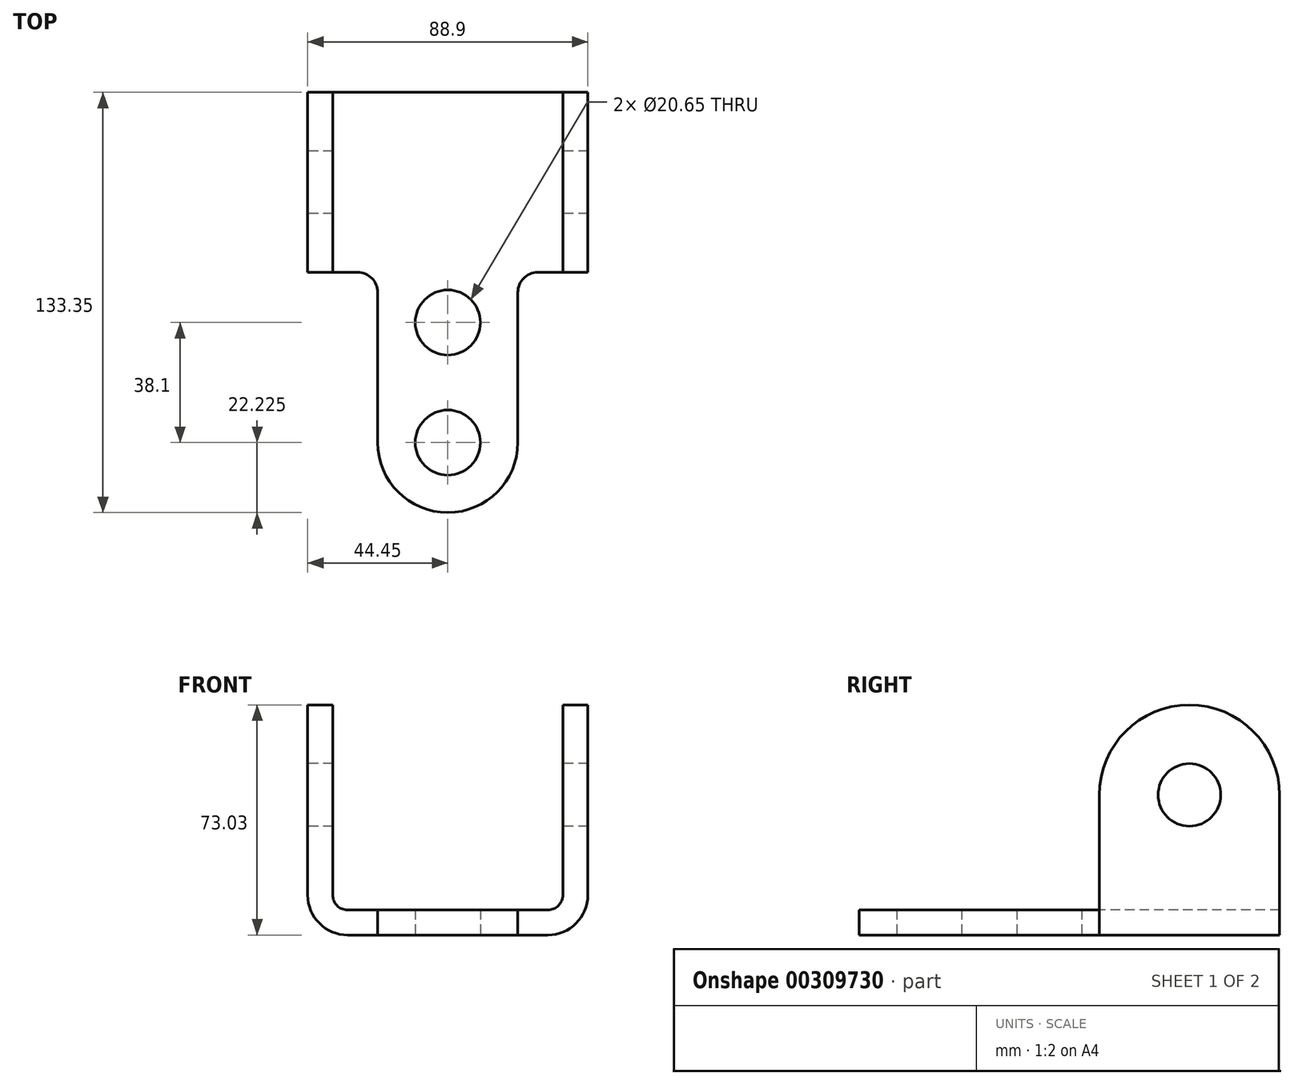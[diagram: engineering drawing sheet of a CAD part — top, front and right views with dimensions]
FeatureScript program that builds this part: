
annotation { "Feature Type Name" : "Feature", "Feature Type Description" : "" }
export const myFeature = defineFeature(function(context is Context, id is Id, definition is map)
    precondition{}
    {
        {
            var Q0;
            Q0=qCreatedBy(makeId("Right.planeOp"),FACE);
            var sketch = newSketch(context, id + "F0", { "sketchPlane" : qUnion([Q0])});
            skLineSegment(sketch, "E0", {"start": v(0, 0) * mm, "end": v(0, 44.45) * mm});
            skLineSegment(sketch, "E1", {"start": v(28.58, 73.03) * mm, "end": v(28.58, 73.03) * mm});
            skLineSegment(sketch, "E2", {"start": v(57.15, 44.45) * mm, "end": v(57.15, 0) * mm});
            skPoint(sketch, "E3.orphan", {"position": v(57.15, 0) * mm});
            skPoint(sketch, "E4.visualSharp", {"position": v(0, 73.03) * mm});
            skArc(sketch, "E4.filletArc", {"start": v(28.58, 73.03) * mm, "mid": v(8.37, 64.66) * mm, "end": v(0, 44.45) * mm});
            skPoint(sketch, "E5.visualSharp", {"position": v(57.15, 73.03) * mm});
            skArc(sketch, "E5.filletArc", {"start": v(57.15, 44.45) * mm, "mid": v(48.78, 64.66) * mm, "end": v(28.58, 73.03) * mm});
            skCircle(sketch, "E6", {"center": v(28.58, 44.45) * mm, "radius": 9.92 * mm});
            skLineSegment(sketch, "E7", {"start": v(0, 0) * mm, "end": v(57.15, 0) * mm});
            skSolve(sketch);
        }
        {
            var Q0;
            Q0 = qSketchRegion(id + "F0", true);
            extrude(context, id + "F1", {"entities" : qUnion([Q0]), "endBound" : BoundingType.SYMMETRIC, "depth" : 88.9 * mm});
        }
        {
            var Q0;
            Q0=qCreatedBy(makeId("Top.planeOp"),FACE);
            var sketch = newSketch(context, id + "F2", { "sketchPlane" : qUnion([Q0])});
            skLineSegment(sketch, "E8.bottom", {"start": v(-22.23, 57.15) * mm, "end": v(22.23, 57.15) * mm});
            skLineSegment(sketch, "E8.top", {"start": v(0, -76.2) * mm, "end": v(0, -76.2) * mm});
            skLineSegment(sketch, "E8.left", {"start": v(-22.23, 57.15) * mm, "end": v(-22.22, -53.97) * mm});
            skLineSegment(sketch, "E8.right", {"start": v(22.22, 57.15) * mm, "end": v(22.23, -53.97) * mm});
            skPoint(sketch, "E9.visualSharp", {"position": v(-22.22, -76.2) * mm});
            skArc(sketch, "E9.filletArc", {"start": v(-22.23, -53.98) * mm, "mid": v(-15.72, -69.7) * mm, "end": v(0, -76.2) * mm});
            skPoint(sketch, "E10.visualSharp", {"position": v(22.22, -76.2) * mm});
            skArc(sketch, "E10.filletArc", {"start": v(0, -76.2) * mm, "mid": v(15.72, -69.7) * mm, "end": v(22.23, -53.98) * mm});
            skCircle(sketch, "E11", {"center": v(0, -53.98) * mm, "radius": 10.33 * mm});
            skCircle(sketch, "E12", {"center": v(0, -15.88) * mm, "radius": 10.33 * mm});
            skSolve(sketch);
        }
        {
            var Q0;
            Q0 = qSketchRegion(id + "F2", true);
            extrude(context, id + "F3", {"entities" : qUnion([Q0]), "operationType" : NewBodyOperationType.ADD, "depth" : 7.94 * mm});
        }
        {
            var Q0;
            Q0=qCreatedBy(makeId("Front.planeOp"),FACE);
            var sketch = newSketch(context, id + "F4", { "sketchPlane" : qUnion([Q0])});
            skLineSegment(sketch, "E13.bottom", {"start": v(-36.51, 84.14) * mm, "end": v(36.51, 84.14) * mm});
            skLineSegment(sketch, "E13.top", {"start": v(-36.51, 7.94) * mm, "end": v(36.51, 7.94) * mm});
            skLineSegment(sketch, "E13.left", {"start": v(-36.51, 84.14) * mm, "end": v(-36.51, 7.94) * mm});
            skLineSegment(sketch, "E13.right", {"start": v(36.51, 84.14) * mm, "end": v(36.51, 7.94) * mm});
            skLineSegment(sketch, "E14", {"start": v(0, 0) * mm, "end": v(0, 82.84) * mm, "construction": true});
            skSolve(sketch);
        }
        {
            var Q0;
            Q0 = qSketchRegion(id + "F4", true);
            extrude(context, id + "F5", {"entities" : qUnion([Q0]), "operationType" : NewBodyOperationType.REMOVE, "endBound" : BoundingType.THROUGH_ALL, "oppositeDirection" : true, "depth" : 25.4 * mm});
        }
        {
            var Q0;
            Q0=makeQuery(id+"F3.boolean.opBoolean","INTERSECT",EDGE,{"derivedFrom":[makeQuery(id+"F1.opExtrude","SWEPT_FACE",FACE,{"disambiguationData":[OSD([sQuery(id+"F0.wireOp",EDGE,"E0")])]}),makeQuery(id+"F3.opExtrude","SWEPT_FACE",FACE,{"disambiguationData":[OSD([sQuery(id+"F2.wireOp",EDGE,"E8.left")])]})]});
            var Q1;
            Q1=makeQuery(id+"F3.boolean.opBoolean","INTERSECT",EDGE,{"derivedFrom":[makeQuery(id+"F1.opExtrude","SWEPT_FACE",FACE,{"disambiguationData":[OSD([sQuery(id+"F0.wireOp",EDGE,"E0")])]}),makeQuery(id+"F3.opExtrude","SWEPT_FACE",FACE,{"disambiguationData":[OSD([sQuery(id+"F2.wireOp",EDGE,"E8.right")])]})]});
            fillet(context, id + "F6", {"entities" : qUnion([Q0, Q1]), "radius" : 6.35 * mm, "tangentPropagation" : true, "allowEdgeOverflow" : false});
        }
        {
            var Q0;
            Q0=makeQuery(id+"F5.boolean.opBoolean","COPY",EDGE,{"derivedFrom":makeQuery(id+"F5.opExtrude","SWEPT_EDGE",EDGE,{"disambiguationData":[OSD([sQuery(id+"F4.wireOp",EDGE,"E13.top"),sQuery(id+"F4.wireOp",EDGE,"E13.left")])]})});
            var Q1;
            Q1=makeQuery(id+"F5.boolean.opBoolean","COPY",EDGE,{"derivedFrom":makeQuery(id+"F5.opExtrude","SWEPT_EDGE",EDGE,{"disambiguationData":[OSD([sQuery(id+"F4.wireOp",EDGE,"E13.top"),sQuery(id+"F4.wireOp",EDGE,"E13.right")])]})});
            fillet(context, id + "F7", {"entities" : qUnion([Q0, Q1]), "radius" : 4.76 * mm, "tangentPropagation" : true, "allowEdgeOverflow" : false});
        }
        {
            var Q0;
            Q0=makeQuery(id+"F1.opExtrude","CAP_EDGE",EDGE,{"disambiguationData":[OSD([sQuery(id+"F0.wireOp",EDGE,"E7")])],"isStart":true});
            var Q1;
            Q1=makeQuery(id+"F1.opExtrude","CAP_EDGE",EDGE,{"disambiguationData":[OSD([sQuery(id+"F0.wireOp",EDGE,"E7")])],"isStart":false});
            fillet(context, id + "F8", {"entities" : qUnion([Q0, Q1]), "radius" : 12.7 * mm, "tangentPropagation" : true, "allowEdgeOverflow" : false});
        }
    });
